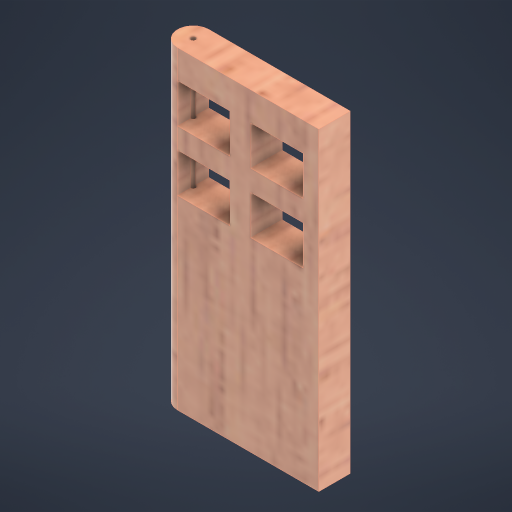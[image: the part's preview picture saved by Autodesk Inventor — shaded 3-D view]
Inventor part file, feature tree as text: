
AUTODESK INVENTOR PART (.ipt)
format: ipt  version: 2023 (Build 270158000, 158)  size: 684,032 bytes
history: native  units: mm
features: sketch x3, other x2, extrude x2, hole x1
ambient origin geometry x8: Origin, YZ Plane, XZ Plane, XY Plane, X Axis, Y Axis, Z Axis, Center Point
bodies: Body1 (feature_tree)
feature tree (8):
  other  "Těleso1"
  extrude  "Vysunutí1"  Depth=30.0mm
  extrude  "Vysunutí2"  Depth=60.0mm
  other  "Plné kulaté zaoblení1"
  hole  "Díra1"  [1 undecoded]
  sketch  "Náčrt1"
  sketch  "Náčrt2"
  sketch  "Náčrt3"
note: 1 required parameter value undecoded (feature->parameter linkage not recoverable at this tier; creation-order binding heuristic only, values carry confidence <= 0.55)
